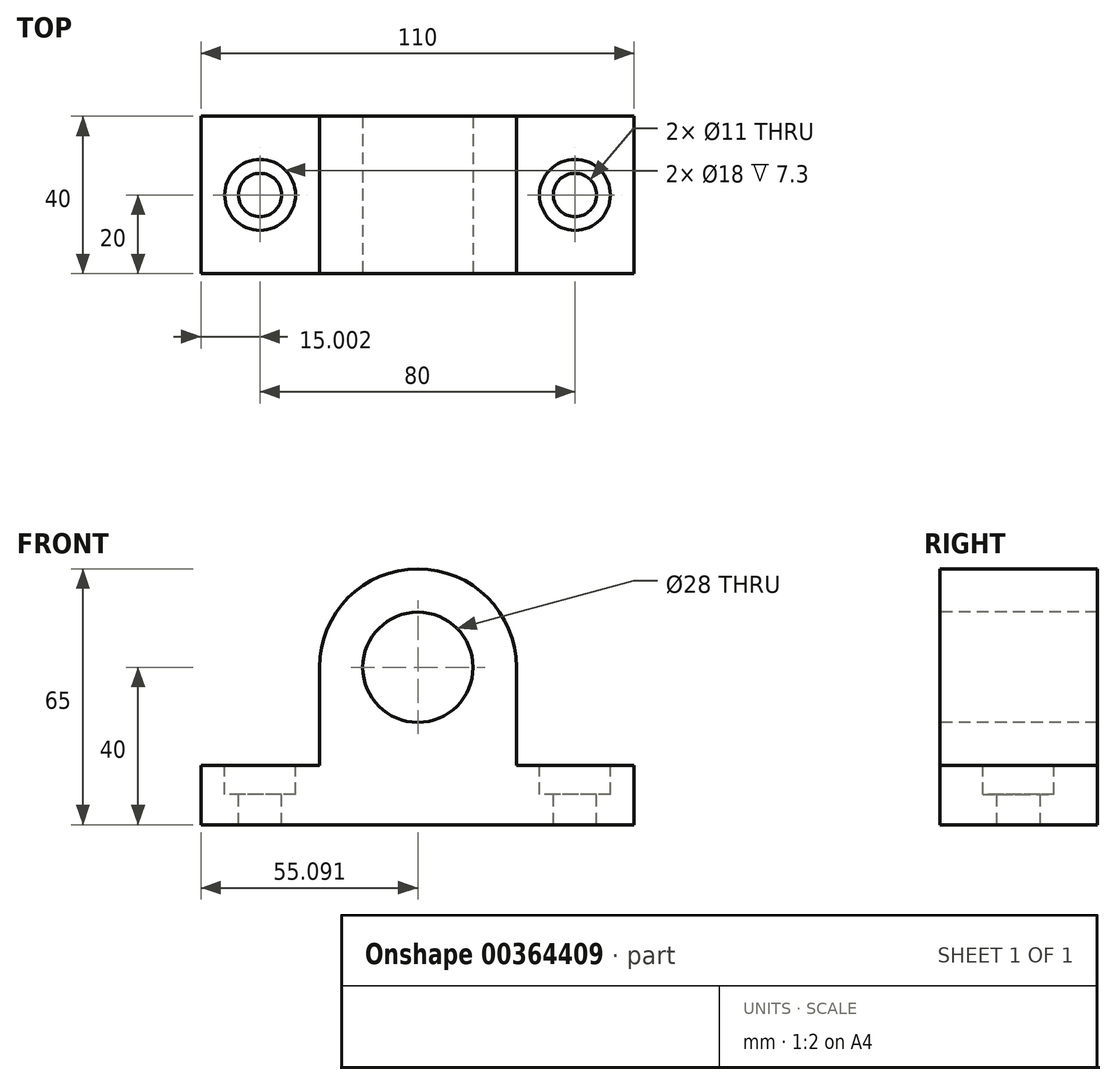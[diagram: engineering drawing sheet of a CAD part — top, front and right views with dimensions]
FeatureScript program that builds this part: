
annotation { "Feature Type Name" : "Feature", "Feature Type Description" : "" }
export const myFeature = defineFeature(function(context is Context, id is Id, definition is map)
    precondition{}
    {
        {
            var Q0;
            Q0=qCreatedBy(makeId("Top.planeOp"),FACE);
            var sketch = newSketch(context, id + "F0", { "sketchPlane" : qUnion([Q0])});
            skLineSegment(sketch, "E0", {"start": v(-50.86, 0) * mm, "end": v(-50.86, 40) * mm});
            skLineSegment(sketch, "E1", {"start": v(59.14, 0) * mm, "end": v(59.14, 40) * mm});
            skLineSegment(sketch, "E2", {"start": v(59.14, 40) * mm, "end": v(-50.86, 40) * mm});
            skLineSegment(sketch, "E3", {"start": v(-50.86, 0) * mm, "end": v(59.14, 0) * mm});
            skSolve(sketch);
        }
        {
            var Q0;
            Q0=qSketchRegion(id+"F0",true);
            extrude(context, id + "F1", {"entities" : qUnion([Q0]), "depth" : 15 * mm});
        }
        {
            var Q0;
            Q0=makeQuery(id+"F1.opExtrude","CAP_FACE",FACE,{"disambiguationData":[OSD([sQuery(id+"F0.wireOp",EDGE,"E0"),sQuery(id+"F0.wireOp",EDGE,"E1"),sQuery(id+"F0.wireOp",EDGE,"E2"),sQuery(id+"F0.wireOp",EDGE,"E3")])],"isStart":false});
            var sketch = newSketch(context, id + "F2", { "sketchPlane" : qUnion([Q0])});
            skCircle(sketch, "E4", {"center": v(-35.86, 20) * mm, "radius": 9 * mm});
            skCircle(sketch, "E5", {"center": v(44.14, 20) * mm, "radius": 9 * mm});
            skSolve(sketch);
        }
        {
            var Q0;
            Q0=sQuery(id+"F2.wireOp",VERTEX,"E4.center");
            var Q1;
            Q1=makeQuery(id+"F1.opExtrude","SWEPT_BODY",BODY,{"disambiguationData":[OSD([sQuery(id+"F0.wireOp",EDGE,"E0"),sQuery(id+"F0.wireOp",EDGE,"E1"),sQuery(id+"F0.wireOp",EDGE,"E2"),sQuery(id+"F0.wireOp",EDGE,"E3")])]});
            hole(context, id + "F3", {"style" : HoleStyle.C_BORE, "endStyle" : HoleEndStyle.THROUGH, "holeDiameter" : 11 * mm, "cBoreDiameter" : 18 * mm, "cBoreDepth" : 7.3 * mm, "isTappedThrough" : true, "tappedDepth" : 12 * mm, "tapClearance" : 3, "startFromSketch" : true, "locations" : qUnion([Q0]), "scope" : qUnion([Q1])});
        }
        {
            var Q0;
            Q0=sQuery(id+"F2.wireOp",VERTEX,"E5.center");
            var Q1;
            Q1=makeQuery(id+"F1.opExtrude","SWEPT_BODY",BODY,{"disambiguationData":[OSD([sQuery(id+"F0.wireOp",EDGE,"E0"),sQuery(id+"F0.wireOp",EDGE,"E1"),sQuery(id+"F0.wireOp",EDGE,"E2"),sQuery(id+"F0.wireOp",EDGE,"E3")])]});
            hole(context, id + "F4", {"style" : HoleStyle.C_BORE, "endStyle" : HoleEndStyle.THROUGH, "holeDiameter" : 11 * mm, "cBoreDiameter" : 18 * mm, "cBoreDepth" : 7.3 * mm, "isTappedThrough" : true, "tappedDepth" : 12 * mm, "tapClearance" : 3, "startFromSketch" : true, "locations" : qUnion([Q0]), "scope" : qUnion([Q1])});
        }
        {
            var Q0;
            Q0=qCreatedBy(makeId("Front.planeOp"),FACE);
            var sketch = newSketch(context, id + "F5", { "sketchPlane" : qUnion([Q0])});
            skLineSegment(sketch, "E6", {"start": v(-20.77, 15.29) * mm, "end": v(-20.77, 40) * mm});
            skLineSegment(sketch, "E7", {"start": v(29.23, 15.29) * mm, "end": v(29.23, 40) * mm});
            skLineSegment(sketch, "E8", {"start": v(0, 40) * mm, "end": v(4.23, 40) * mm});
            skPoint(sketch, "E9.end.orphan", {"position": v(-50.77, 15.29) * mm});
            skPoint(sketch, "E10.start.orphan", {"position": v(-50.77, 0) * mm});
            skPoint(sketch, "E11.end.orphan", {"position": v(59.23, 15.29) * mm});
            skPoint(sketch, "E11.start.orphan", {"position": v(59.04, 0) * mm});
            skLineSegment(sketch, "E12", {"start": v(-20.77, 15.29) * mm, "end": v(-20.77, 0) * mm});
            skLineSegment(sketch, "E13", {"start": v(29.23, 15.29) * mm, "end": v(29.23, 0) * mm});
            skLineSegment(sketch, "E14", {"start": v(29.23, 0) * mm, "end": v(-20.77, 0) * mm});
            skCircle(sketch, "E15", {"center": v(4.23, 40) * mm, "radius": 14 * mm});
            skArc(sketch, "E16", {"start": v(29.23, 40) * mm, "mid": v(4.23, 65) * mm, "end": v(-20.77, 40) * mm});
            skSolve(sketch);
        }
        {
            var Q0;
            Q0=qSketchRegion(id+"F5",true);
            extrude(context, id + "F6", {"entities" : qUnion([Q0]), "operationType" : NewBodyOperationType.ADD, "oppositeDirection" : true, "depth" : 40 * mm});
        }
    });
